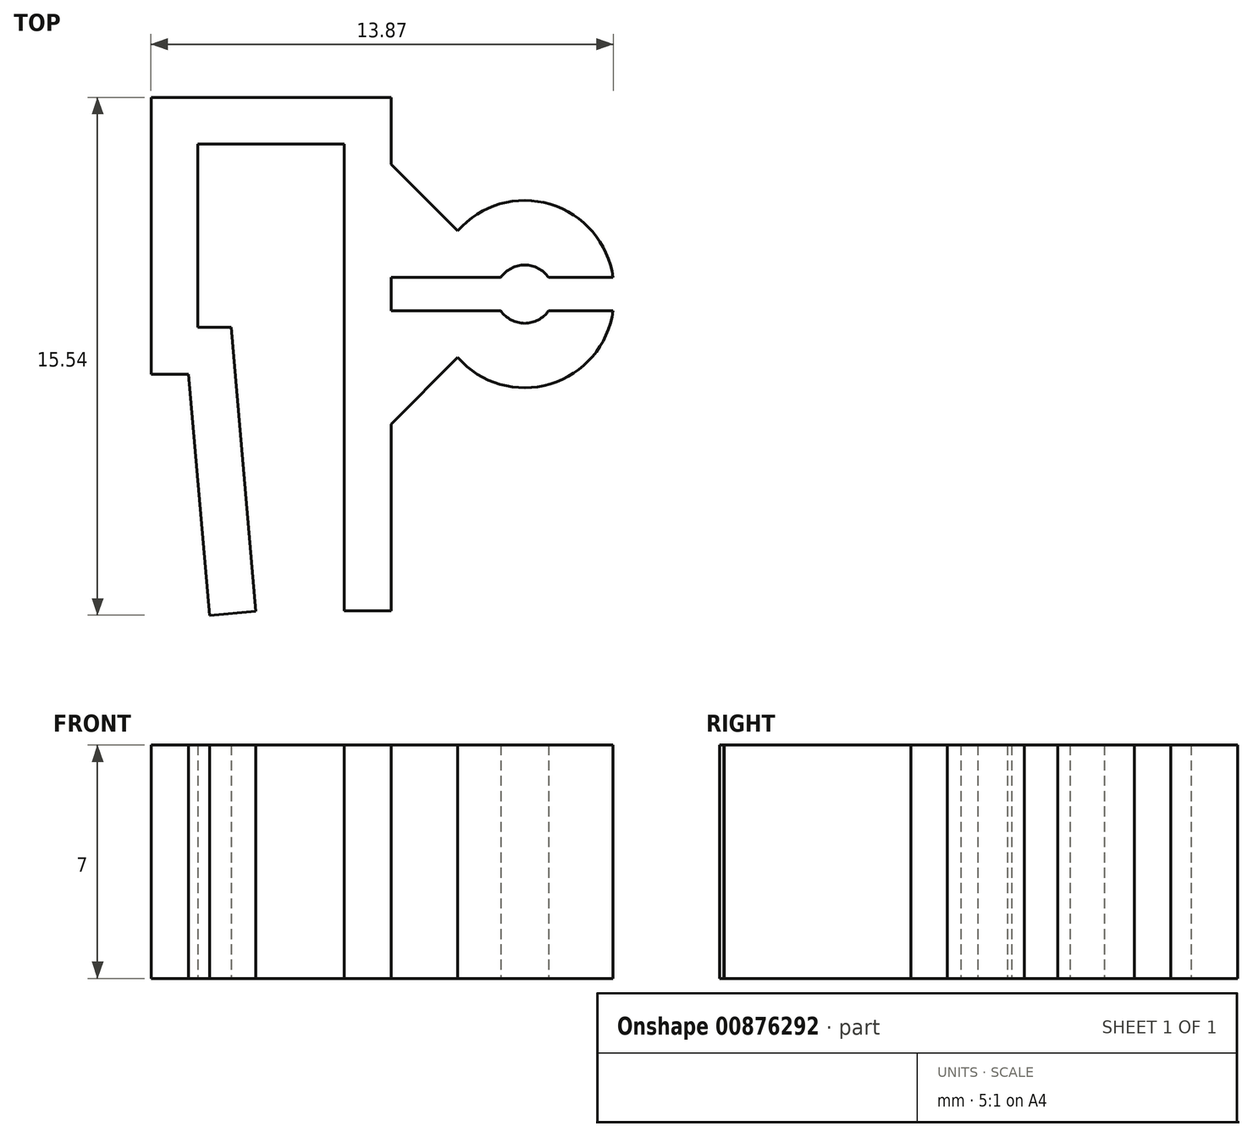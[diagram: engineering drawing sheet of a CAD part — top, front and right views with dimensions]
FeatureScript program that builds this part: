
annotation { "Feature Type Name" : "Feature", "Feature Type Description" : "" }
export const myFeature = defineFeature(function(context is Context, id is Id, definition is map)
    precondition{}
    {
        {
            var Q0;
            Q0=qCreatedBy(makeId("Top.planeOp"),FACE);
            var sketch = newSketch(context, id + "F0", { "sketchPlane" : qUnion([Q0])});
            skLineSegment(sketch, "E0.bottom", {"start": v(-25.48, 45.84) * mm, "end": v(-21.08, 45.84) * mm});
            skLineSegment(sketch, "E0.left", {"start": v(-25.48, 45.84) * mm, "end": v(-25.48, 40.34) * mm});
            skLineSegment(sketch, "E0.right", {"start": v(-21.08, 45.84) * mm, "end": v(-21.08, 33.84) * mm});
            skPoint(sketch, "E1", {"position": v(-24.48, 40.34) * mm});
            skLineSegment(sketch, "E2", {"start": v(-24.48, 40.34) * mm, "end": v(-25.48, 40.34) * mm});
            skLineSegment(sketch, "E3", {"start": v(-24.48, 40.34) * mm, "end": v(-23.9, 33.81) * mm});
            skLineSegment(sketch, "E4.0", {"start": v(-19.68, 47.24) * mm, "end": v(-19.68, 45.24) * mm});
            skLineSegment(sketch, "E4.1", {"start": v(-25.76, 38.94) * mm, "end": v(-25.3, 33.69) * mm});
            skLineSegment(sketch, "E4.2", {"start": v(-25.76, 38.94) * mm, "end": v(-26.88, 38.94) * mm});
            skLineSegment(sketch, "E4.3", {"start": v(-26.88, 47.24) * mm, "end": v(-26.88, 38.94) * mm});
            skLineSegment(sketch, "E4.4", {"start": v(-26.88, 47.24) * mm, "end": v(-19.68, 47.24) * mm});
            skArc(sketch, "E5", {"start": v(-13.65, 43.24) * mm, "mid": v(-15.66, 44.15) * mm, "end": v(-17.68, 43.24) * mm});
            skArc(sketch, "E6", {"start": v(-13.01, 41.84) * mm, "mid": v(-14.9, 44.03) * mm, "end": v(-17.68, 43.24) * mm});
            skLineSegment(sketch, "E7", {"start": v(-19.68, 41.34) * mm, "end": v(-13.01, 41.34) * mm, "construction": true});
            skArc(sketch, "E8.MirrorCS", {"start": v(-13.01, 40.84) * mm, "mid": v(-14.9, 38.64) * mm, "end": v(-17.68, 39.44) * mm});
            skPoint(sketch, "E9.MirrorCS.end.orphan", {"position": v(-13.01, 40.84) * mm});
            skLineSegment(sketch, "E10", {"start": v(-13.01, 41.84) * mm, "end": v(-14.95, 41.84) * mm});
            skLineSegment(sketch, "E11", {"start": v(-13.01, 40.84) * mm, "end": v(-14.95, 40.84) * mm});
            skArc(sketch, "E12", {"start": v(-16.38, 40.84) * mm, "mid": v(-15.66, 40.46) * mm, "end": v(-14.95, 40.84) * mm});
            skArc(sketch, "E13.trimOffspring", {"start": v(-14.95, 41.84) * mm, "mid": v(-15.66, 42.21) * mm, "end": v(-16.38, 41.84) * mm});
            skLineSegment(sketch, "E14.trimOffspring", {"start": v(-16.38, 40.84) * mm, "end": v(-19.68, 40.84) * mm});
            skLineSegment(sketch, "E15.trimOffspring", {"start": v(-16.38, 41.84) * mm, "end": v(-19.68, 41.84) * mm});
            skLineSegment(sketch, "E16", {"start": v(-17.68, 43.24) * mm, "end": v(-19.68, 45.24) * mm});
            skLineSegment(sketch, "E17", {"start": v(-17.68, 39.44) * mm, "end": v(-19.68, 37.44) * mm});
            skPoint(sketch, "E18.start.orphan", {"position": v(-19.68, 43.24) * mm});
            skLineSegment(sketch, "E19.trimOffspring", {"start": v(-19.68, 41.84) * mm, "end": v(-19.68, 40.84) * mm});
            skLineSegment(sketch, "E20.trimOffspring", {"start": v(-19.68, 37.44) * mm, "end": v(-19.68, 33.84) * mm});
            skPoint(sketch, "E21.MirrorCS.end.orphan", {"position": v(-17.68, 39.44) * mm});
            skPoint(sketch, "E21.MirrorCS.start.orphan", {"position": v(-19.68, 39.44) * mm});
            skLineSegment(sketch, "E22", {"start": v(-19.68, 33.84) * mm, "end": v(-19.68, 31.84) * mm});
            skLineSegment(sketch, "E23", {"start": v(-19.68, 31.84) * mm, "end": v(-21.08, 31.84) * mm});
            skLineSegment(sketch, "E24", {"start": v(-21.08, 31.84) * mm, "end": v(-21.08, 33.84) * mm});
            skLineSegment(sketch, "E25", {"start": v(-23.9, 33.81) * mm, "end": v(-23.73, 31.82) * mm});
            skLineSegment(sketch, "E26", {"start": v(-25.3, 33.69) * mm, "end": v(-25.13, 31.7) * mm});
            skLineSegment(sketch, "E27", {"start": v(-23.73, 31.82) * mm, "end": v(-25.13, 31.7) * mm});
            skSolve(sketch);
        }
        {
            var Q0;
            Q0=makeQuery(id+"F0.imprint","IMPRINT",FACE,{"disambiguationData":[TD([[makeQuery(id+"F0.imprint","IMPRINT",EDGE,{"derivedFrom":sQuery(id+"F0.wireOp",EDGE,"E0.bottom")}),1.0]])]});
            extrude(context, id + "F1", {"entities" : qUnion([Q0]), "depth" : 7 * mm, "offsetDistance" : 25 * mm});
        }
    });
